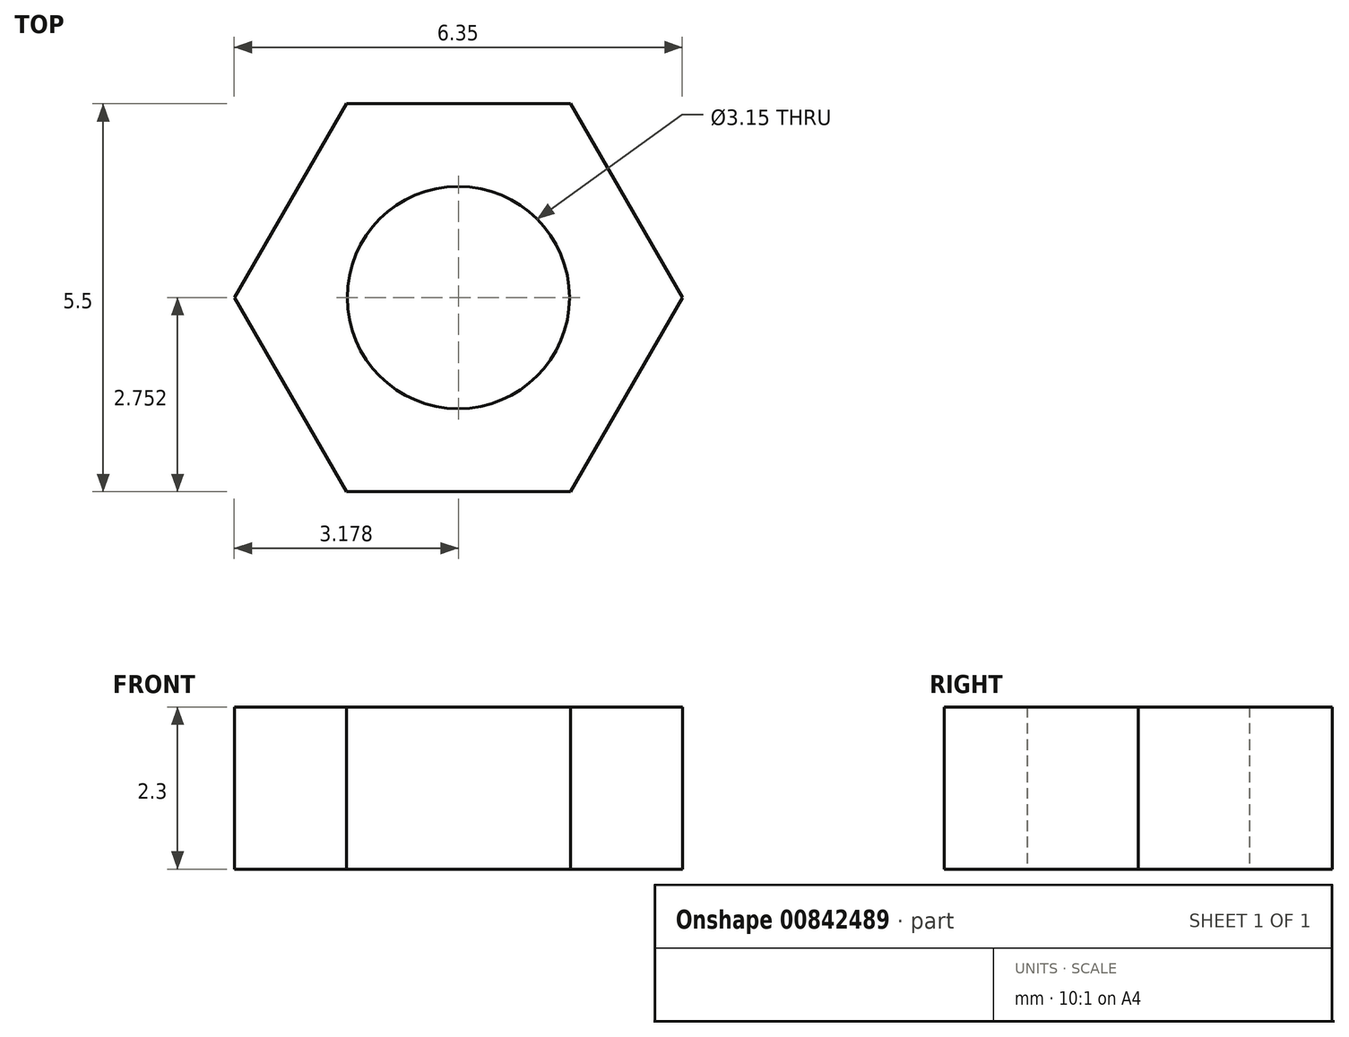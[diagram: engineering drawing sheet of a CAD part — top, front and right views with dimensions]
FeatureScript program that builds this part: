
annotation { "Feature Type Name" : "Feature", "Feature Type Description" : "" }
export const myFeature = defineFeature(function(context is Context, id is Id, definition is map)
    precondition{}
    {
        {
            var Q0;
            Q0=qCreatedBy(makeId("Top.planeOp"),FACE);
            var sketch = newSketch(context, id + "F0", { "sketchPlane" : qUnion([Q0])});
            skCircle(sketch, "E0.cCircle", {"center": v(-1.16, 1.16) * mm, "radius": 3.18 * mm, "construction": true});
            skLineSegment(sketch, "E0.0", {"start": v(0.43, 3.91) * mm, "end": v(2.01, 1.16) * mm});
            skLineSegment(sketch, "E0.1", {"start": v(2.01, 1.16) * mm, "end": v(0.43, -1.59) * mm});
            skLineSegment(sketch, "E0.2", {"start": v(0.43, -1.59) * mm, "end": v(-2.75, -1.59) * mm});
            skLineSegment(sketch, "E0.3", {"start": v(-2.75, -1.59) * mm, "end": v(-4.34, 1.16) * mm});
            skLineSegment(sketch, "E0.4", {"start": v(-4.34, 1.16) * mm, "end": v(-2.75, 3.91) * mm});
            skLineSegment(sketch, "E0.5", {"start": v(-2.75, 3.91) * mm, "end": v(0.43, 3.91) * mm});
            skSolve(sketch);
        }
        {
            var Q0;
            Q0=qSketchRegion(id+"F0",true);
            extrude(context, id + "F1", {"entities" : qUnion([Q0]), "depth" : (3.9 - 1.6) * mm, "offsetDistance" : 25 * mm});
        }
        {
            var Q0;
            Q0=sQuery(id+"F0.wireOp",VERTEX,"E0.cCircle.center");
            var Q1;
            Q1=makeQuery(id+"F1.opExtrude","SWEPT_BODY",BODY,{"disambiguationData":[OSD([sQuery(id+"F0.wireOp",EDGE,"E0.0"),sQuery(id+"F0.wireOp",EDGE,"E0.1"),sQuery(id+"F0.wireOp",EDGE,"E0.2"),sQuery(id+"F0.wireOp",EDGE,"E0.3"),sQuery(id+"F0.wireOp",EDGE,"E0.4"),sQuery(id+"F0.wireOp",EDGE,"E0.5")])]});
            hole(context, id + "F2", {"style" : HoleStyle.SIMPLE, "endStyle" : HoleEndStyle.THROUGH, "oppositeDirection" : true, "standardTappedOrClearance" : lookupTablePath({ "standard" : "ISO", "fit" : "Close", "size" : "M3", "type" : "Clearance" }), "standardBlindInLast" : lookupTablePath({ "fit" : "Close", "standard" : "ISO", "size" : "M3", "type" : "Clearance" }), "holeDiameter" : 3.15 * mm, "majorDiameter" : 5 * mm, "isTappedThrough" : true, "tappedDepth" : 12 * mm, "tapClearance" : 3, "locations" : qUnion([Q0]), "scope" : qUnion([Q1])});
        }
    });
